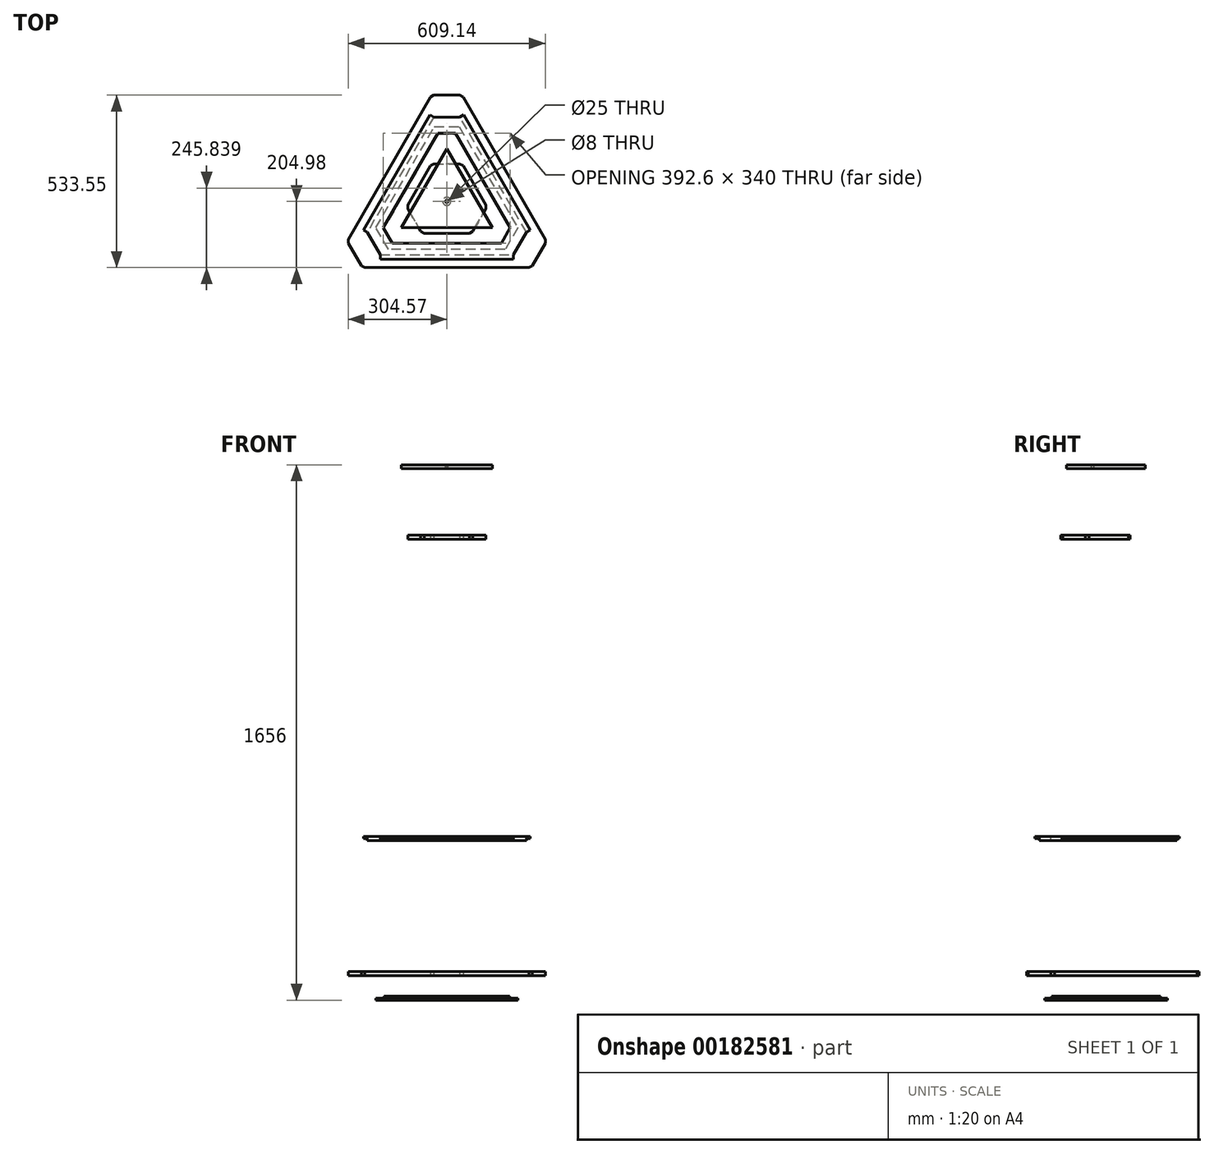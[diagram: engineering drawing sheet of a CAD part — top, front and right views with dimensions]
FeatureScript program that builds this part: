
annotation { "Feature Type Name" : "Feature", "Feature Type Description" : "" }
export const myFeature = defineFeature(function(context is Context, id is Id, definition is map)
    precondition{}
    {
        {
            var Q0;
            Q0=qCreatedBy(makeId("Front.planeOp"),FACE);
            var sketch = newSketch(context, id + "F0", { "sketchPlane" : qUnion([Q0])});
            skLineSegment(sketch, "E0", {"start": v(-375, 0) * mm, "end": v(375, 0) * mm});
            skLineSegment(sketch, "E1", {"start": v(0, 0) * mm, "end": v(0, 1650) * mm});
            skLineSegment(sketch, "E2", {"start": v(-150, 1650) * mm, "end": v(150, 1650) * mm});
            skSolve(sketch);
        }
        {
            var Q0;
            Q0=sQuery(id+"F0.wireOp",EDGE,"E2");
            cPoint(context, id + "F1", {"entities" : qUnion([Q0]), "parameter" : 0.5});
        }
        {
            var Q0;
            Q0=qCreatedBy(id+"F1",VERTEX);
            var Q1;
            Q1=sQuery(id+"F0.wireOp",EDGE,"E1");
            cPlane(context, id + "F2", {"entities" : qUnion([Q0, Q1]), "cplaneType" : CPlaneType.LINE_POINT, "offset" : 25 * mm, "width" : 150 * mm, "height" : 150 * mm});
        }
        {
            var Q0;
            Q0=qCreatedBy(makeId("Top.planeOp"),FACE);
            var sketch = newSketch(context, id + "F3", { "sketchPlane" : qUnion([Q0])});
            skCircle(sketch, "E3.cCircle", {"center": v(0, 0) * mm, "radius": 216.5 * mm, "construction": true});
            skLineSegment(sketch, "E3.0", {"start": v(375, -216.5) * mm, "end": v(-375, -216.5) * mm});
            skLineSegment(sketch, "E3.1", {"start": v(-375, -216.5) * mm, "end": v(0, 433.01) * mm});
            skLineSegment(sketch, "E3.2", {"start": v(0, 433.01) * mm, "end": v(375, -216.5) * mm});
            skPoint(sketch, "E3.0.midPoint", {"position": v(0, -216.5) * mm});
            skSolve(sketch);
        }
        {
            var Q0;
            Q0=qCreatedBy(id+"F2.planeOp",FACE);
            var sketch = newSketch(context, id + "F4", { "sketchPlane" : qUnion([Q0])});
            skCircle(sketch, "E4.cCircle", {"center": v(0, 0) * mm, "radius": 86.6 * mm, "construction": true});
            skLineSegment(sketch, "E4.0", {"start": v(150, -86.6) * mm, "end": v(-150, -86.6) * mm});
            skLineSegment(sketch, "E4.1", {"start": v(-150, -86.6) * mm, "end": v(0, 173.2) * mm});
            skLineSegment(sketch, "E4.2", {"start": v(0, 173.2) * mm, "end": v(150, -86.6) * mm});
            skPoint(sketch, "E4.0.midPoint", {"position": v(0, -86.6) * mm});
            skSolve(sketch);
        }
        {
            var Q0;
            Q0=makeQuery(id+"F3.imprint","IMPRINT",FACE,{"disambiguationData":[TD([[makeQuery(id+"F3.imprint","IMPRINT",EDGE,{"derivedFrom":sQuery(id+"F3.wireOp",EDGE,"E3.0")}),-1.0]])]});
            var Q1;
            Q1=makeQuery(id+"F4.imprint","IMPRINT",FACE,{"disambiguationData":[TD([[makeQuery(id+"F4.imprint","IMPRINT",EDGE,{"derivedFrom":sQuery(id+"F4.wireOp",EDGE,"E4.0")}),-1.0]])]});
            loft(context, id + "F5", {"sheetProfilesArray" : [{ "sheetProfileEntities" : qUnion([Q0]) }, { "sheetProfileEntities" : qUnion([Q1]) }]});
        }
        {
            var Q0;
            {var subQ0=sQuery(id+"F4.wireOp",EDGE,"E4.0");var subQ1=sQuery(id+"F4.wireOp",EDGE,"E4.1");var subQ2=sQuery(id+"F4.wireOp",EDGE,"E4.2");var subQ3=sQuery(id+"F3.wireOp",EDGE,"E3.0");var subQ4=sQuery(id+"F3.wireOp",EDGE,"E3.1");var subQ5=sQuery(id+"F3.wireOp",EDGE,"E3.2");Q0=makeQuery(id+"F5.opLoft","SWEPT_FACE",FACE,{"disambiguationData":[OSD([subQ3,subQ4,subQ5,subQ0,subQ1,subQ2]),TDD([makeQuery(id+"F3.imprint","INTERSECT",VERTEX,{"derivedFrom":[subQ3,subQ5]}),makeQuery(id+"F3.imprint","INTERSECT",VERTEX,{"derivedFrom":[subQ3,subQ4]}),makeQuery(id+"F3.imprint","IMPRINT",EDGE,{"derivedFrom":subQ3}),makeQuery(id+"F4.imprint","INTERSECT",VERTEX,{"derivedFrom":[subQ0,subQ2]}),makeQuery(id+"F4.imprint","INTERSECT",VERTEX,{"derivedFrom":[subQ0,subQ1]}),makeQuery(id+"F4.imprint","IMPRINT",EDGE,{"derivedFrom":subQ0})])]});}
            cPlane(context, id + "F6", {"entities" : qUnion([Q0]), "cplaneType" : CPlaneType.OFFSET, "offset" : 12 * mm, "oppositeDirection" : true, "width" : 150 * mm, "height" : 150 * mm});
        }
        {
            var Q0;
            Q0=qCreatedBy(id+"F6.planeOp",FACE);
            var sketch = newSketch(context, id + "F7", { "sketchPlane" : qUnion([Q0])});
            skCircle(sketch, "E5", {"center": v(0, 812.97) * mm, "radius": 960.24 * mm});
            skSolve(sketch);
        }
        {
            var Q0;
            Q0=qSketchRegion(id+"F7",true);
            extrude(context, id + "F8", {"entities" : qUnion([Q0]), "operationType" : NewBodyOperationType.REMOVE, "endBound" : BoundingType.THROUGH_ALL, "oppositeDirection" : true, "depth" : 25 * mm});
        }
        {
            var Q0;
            Q0=makeQuery(id+"F5.opLoft","CAP_FACE",FACE,{"disambiguationData":[OSD([makeQuery(id+"F4.imprint","IMPRINT",FACE,{"disambiguationData":[TD([[makeQuery(id+"F4.imprint","IMPRINT",EDGE,{"derivedFrom":sQuery(id+"F4.wireOp",EDGE,"E4.0")}),-1.0]])]})])],"isStart":true});
            var sketch = newSketch(context, id + "F9", { "sketchPlane" : qUnion([Q0])});
            skLineSegment(sketch, "E6", {"start": v(150, -86.6) * mm, "end": v(129.15, -74.57) * mm});
            skLineSegment(sketch, "E7", {"start": v(-150, -86.6) * mm, "end": v(-129.15, -74.57) * mm});
            skSolve(sketch);
        }
        {
            var Q0;
            Q0=makeQuery(id+"F5.opLoft","SWEPT_EDGE",EDGE,{"disambiguationData":[OSD([sQuery(id+"F3.wireOp",EDGE,"E3.0"),sQuery(id+"F3.wireOp",EDGE,"E3.1"),sQuery(id+"F4.wireOp",EDGE,"E4.0"),sQuery(id+"F4.wireOp",EDGE,"E4.1")])]});
            var Q1;
            Q1=sQuery(id+"F9.wireOp",EDGE,"E7");
            cPlane(context, id + "F10", {"entities" : qUnion([Q0, Q1]), "cplaneType" : CPlaneType.LINE_ANGLE, "offset" : 25 * mm, "angle" : 0 * degree, "width" : 150 * mm, "height" : 150 * mm});
        }
        {
            var Q0;
            Q0=makeQuery(id+"F5.opLoft","SWEPT_EDGE",EDGE,{"disambiguationData":[OSD([sQuery(id+"F3.wireOp",EDGE,"E3.0"),sQuery(id+"F3.wireOp",EDGE,"E3.2"),sQuery(id+"F4.wireOp",EDGE,"E4.0"),sQuery(id+"F4.wireOp",EDGE,"E4.2")])]});
            var Q1;
            Q1=sQuery(id+"F9.wireOp",EDGE,"E6");
            cPlane(context, id + "F11", {"entities" : qUnion([Q0, Q1]), "cplaneType" : CPlaneType.LINE_ANGLE, "offset" : 25 * mm, "angle" : 0 * degree, "width" : 150 * mm, "height" : 150 * mm});
        }
        {
            var Q0;
            Q0=qCreatedBy(id+"F11.planeOp",FACE);
            var sketch = newSketch(context, id + "F12", { "sketchPlane" : qUnion([Q0])});
            skCircle(sketch, "E8", {"center": v(304.07, 817.21) * mm, "radius": 870.23 * mm});
            skSolve(sketch);
        }
        {
            var Q0;
            Q0=qSketchRegion(id+"F12",true);
            extrude(context, id + "F13", {"entities" : qUnion([Q0]), "operationType" : NewBodyOperationType.REMOVE, "oppositeDirection" : true, "depth" : 25 * mm});
        }
        {
            var Q0;
            Q0=qCreatedBy(id+"F10.planeOp",FACE);
            var sketch = newSketch(context, id + "F14", { "sketchPlane" : qUnion([Q0])});
            skCircle(sketch, "E9", {"center": v(291.65, 811.12) * mm, "radius": 892.94 * mm});
            skSolve(sketch);
        }
        {
            var Q0;
            Q0=qSketchRegion(id+"F14",true);
            extrude(context, id + "F15", {"entities" : qUnion([Q0]), "operationType" : NewBodyOperationType.REMOVE, "depth" : 25 * mm});
        }
        {
            var Q0;
            Q0=makeQuery(id+"F8.boolean.opBoolean","COPY",FACE,{"derivedFrom":makeQuery(id+"F8.opExtrude","CAP_FACE",FACE,{"disambiguationData":[OSD([sQuery(id+"F7.wireOp",EDGE,"E5")])],"isStart":true})});
            cPlane(context, id + "F16", {"entities" : qUnion([Q0]), "cplaneType" : CPlaneType.OFFSET, "offset" : 6 * mm, "oppositeDirection" : true, "width" : 150 * mm, "height" : 150 * mm});
        }
        {
            var Q0;
            Q0=qCreatedBy(makeId("Front.planeOp"),FACE);
            var sketch = newSketch(context, id + "F17", { "sketchPlane" : qUnion([Q0])});
            skLineSegment(sketch, "E10.0.0", {"start": v(-354.15, 0) * mm, "end": v(-129.15, 1650) * mm, "construction": true});
            skLineSegment(sketch, "E10.0.1", {"start": v(-129.15, 1650) * mm, "end": v(129.15, 1650) * mm});
            skLineSegment(sketch, "E10.0.2", {"start": v(129.15, 1650) * mm, "end": v(354.15, 0) * mm, "construction": true});
            skLineSegment(sketch, "E11.0", {"start": v(-375, 0) * mm, "end": v(-150, 1650) * mm, "construction": true});
            skLineSegment(sketch, "E12.0", {"start": v(375, 0) * mm, "end": v(150, 1650) * mm, "construction": true});
            skLineSegment(sketch, "E13", {"start": v(83.17, 1400) * mm, "end": v(205.9, 500) * mm});
            skLineSegment(sketch, "E14", {"start": v(-83.17, 1400) * mm, "end": v(-205.9, 500) * mm});
            skLineSegment(sketch, "E15", {"start": v(83.17, 1400) * mm, "end": v(-83.17, 1400) * mm});
            skLineSegment(sketch, "E16", {"start": v(205.9, 500) * mm, "end": v(-205.9, 500) * mm});
            skLineSegment(sketch, "E17", {"start": v(274.07, 0) * mm, "end": v(267.26, 50) * mm});
            skLineSegment(sketch, "E18", {"start": v(267.26, 50) * mm, "end": v(-267.26, 50) * mm});
            skLineSegment(sketch, "E19", {"start": v(-267.26, 50) * mm, "end": v(-274.07, 0) * mm});
            skLineSegment(sketch, "E20", {"start": v(274.07, 0) * mm, "end": v(-274.07, 0) * mm});
            skSolve(sketch);
        }
        {
            var Q0;
            Q0=makeQuery(id+"F17.imprint","IMPRINT",FACE,{"disambiguationData":[TD([[makeQuery(id+"F17.imprint","IMPRINT",EDGE,{"derivedFrom":sQuery(id+"F17.wireOp",EDGE,"E13")}),-1.0]])]});
            var Q1;
            Q1=makeQuery(id+"F17.imprint","IMPRINT",FACE,{"disambiguationData":[TD([[makeQuery(id+"F17.imprint","IMPRINT",EDGE,{"derivedFrom":sQuery(id+"F17.wireOp",EDGE,"E17")}),1.0]])]});
            extrude(context, id + "F18", {"entities" : qUnion([Q0, Q1]), "operationType" : NewBodyOperationType.REMOVE, "endBound" : BoundingType.THROUGH_ALL, "depth" : 25 * mm});
        }
        {
            var Q0;
            Q0=qCreatedBy(makeId("Front.planeOp"),FACE);
            var sketch = newSketch(context, id + "F19", { "sketchPlane" : qUnion([Q0])});
            skLineSegment(sketch, "E21.0.0", {"start": v(274.07, 0) * mm, "end": v(267.26, 50) * mm});
            skLineSegment(sketch, "E21.0.1", {"start": v(267.26, 50) * mm, "end": v(-267.26, 50) * mm});
            skLineSegment(sketch, "E21.0.2", {"start": v(-267.26, 50) * mm, "end": v(-274.07, 0) * mm});
            skLineSegment(sketch, "E21.0.3", {"start": v(-274.07, 0) * mm, "end": v(-354.15, 0) * mm});
            skLineSegment(sketch, "E21.0.4", {"start": v(-354.15, 0) * mm, "end": v(-129.15, 1650) * mm});
            skLineSegment(sketch, "E21.0.5", {"start": v(-129.15, 1650) * mm, "end": v(129.15, 1650) * mm});
            skLineSegment(sketch, "E21.0.6", {"start": v(129.15, 1650) * mm, "end": v(354.15, 0) * mm});
            skLineSegment(sketch, "E21.0.7", {"start": v(354.15, 0) * mm, "end": v(274.07, 0) * mm});
            skLineSegment(sketch, "E22.0", {"start": v(205.9, 500) * mm, "end": v(83.17, 1400) * mm});
            skLineSegment(sketch, "E22.1", {"start": v(-205.9, 500) * mm, "end": v(-83.17, 1400) * mm});
            skLineSegment(sketch, "E23", {"start": v(205.9, 500) * mm, "end": v(-205.9, 500) * mm});
            skLineSegment(sketch, "E24", {"start": v(262.9, 82) * mm, "end": v(-262.9, 82) * mm});
            skLineSegment(sketch, "E25", {"start": v(80.44, 1420) * mm, "end": v(-80.44, 1420) * mm});
            skLineSegment(sketch, "E26", {"start": v(130.79, 1638) * mm, "end": v(-130.79, 1638) * mm});
            skLineSegment(sketch, "E27", {"start": v(78.8, 1432) * mm, "end": v(-78.8, 1432) * mm});
            skLineSegment(sketch, "E28", {"start": v(207.53, 488) * mm, "end": v(-207.53, 488) * mm});
            skLineSegment(sketch, "E29", {"start": v(264.53, 70) * mm, "end": v(-264.53, 70) * mm});
            skLineSegment(sketch, "E30", {"start": v(205.9, 500) * mm, "end": v(285.97, 500) * mm});
            skLineSegment(sketch, "E31", {"start": v(207.53, 488) * mm, "end": v(287.6, 488) * mm});
            skLineSegment(sketch, "E32", {"start": v(-207.53, 488) * mm, "end": v(-287.6, 488) * mm});
            skLineSegment(sketch, "E33", {"start": v(-205.9, 500) * mm, "end": v(-285.97, 500) * mm});
            skLineSegment(sketch, "E34", {"start": v(262.9, 82) * mm, "end": v(342.97, 82) * mm});
            skLineSegment(sketch, "E35", {"start": v(264.53, 70) * mm, "end": v(344.6, 70) * mm});
            skLineSegment(sketch, "E36", {"start": v(-264.53, 70) * mm, "end": v(-344.6, 70) * mm});
            skLineSegment(sketch, "E37", {"start": v(-262.9, 82) * mm, "end": v(-342.97, 82) * mm});
            skLineSegment(sketch, "E38", {"start": v(-80.44, 1420) * mm, "end": v(-160.51, 1420) * mm});
            skLineSegment(sketch, "E39", {"start": v(80.44, 1420) * mm, "end": v(160.51, 1420) * mm});
            skLineSegment(sketch, "E40", {"start": v(78.8, 1432) * mm, "end": v(158.88, 1432) * mm});
            skLineSegment(sketch, "E41", {"start": v(-78.8, 1432) * mm, "end": v(-158.88, 1432) * mm});
            skSolve(sketch);
        }
        {
            var Q0;
            Q0=makeQuery(id+"F18.boolean.opBoolean","COPY",FACE,{"derivedFrom":makeQuery(id+"F18.opExtrude","SWEPT_FACE",FACE,{"disambiguationData":[OSD([sQuery(id+"F17.wireOp",EDGE,"E16")])]})});
            var Q1;
            Q1=sQuery(id+"F19.wireOp",EDGE,"E23");
            cPlane(context, id + "F20", {"entities" : qUnion([Q0, Q1]), "cplaneType" : CPlaneType.LINE_ANGLE, "offset" : 25 * mm, "angle" : 0 * degree, "width" : 150 * mm, "height" : 150 * mm});
        }
        {
            var Q0;
            Q0=qCreatedBy(id+"F20.planeOp",FACE);
            var sketch = newSketch(context, id + "F21", { "sketchPlane" : qUnion([Q0])});
            skCircle(sketch, "E42.cCircle", {"center": v(0, 0) * mm, "radius": 165.1 * mm, "construction": true});
            skLineSegment(sketch, "E42.0", {"start": v(-285.97, 165.1) * mm, "end": v(285.97, 165.1) * mm, "construction": true});
            skLineSegment(sketch, "E42.1", {"start": v(285.97, 165.1) * mm, "end": v(0, -330.2) * mm, "construction": true});
            skLineSegment(sketch, "E42.2", {"start": v(0, -330.2) * mm, "end": v(-285.97, 165.1) * mm, "construction": true});
            skPoint(sketch, "E42.0.midPoint", {"position": v(0, 165.1) * mm});
            skLineSegment(sketch, "E43", {"start": v(-285.97, 165.1) * mm, "end": v(-285.97, 0) * mm, "construction": true});
            skLineSegment(sketch, "E44", {"start": v(-205.9, 0) * mm, "end": v(-205.9, 165.1) * mm, "construction": true});
            skLineSegment(sketch, "E45", {"start": v(-285.94, 171.12) * mm, "end": v(264.96, 171.12) * mm, "construction": true});
            skLineSegment(sketch, "E46", {"start": v(-205.9, 165.1) * mm, "end": v(-245.93, 95.76) * mm});
            skCircle(sketch, "E47.cCircle", {"center": v(0, 0) * mm, "radius": 171.12 * mm, "construction": true});
            skLineSegment(sketch, "E47.0", {"start": v(-296.4, 171.12) * mm, "end": v(296.4, 171.12) * mm, "construction": true});
            skLineSegment(sketch, "E47.1", {"start": v(296.4, 171.12) * mm, "end": v(0, -342.25) * mm, "construction": true});
            skLineSegment(sketch, "E47.2", {"start": v(0, -342.25) * mm, "end": v(-296.4, 171.12) * mm, "construction": true});
            skPoint(sketch, "E47.0.midPoint", {"position": v(0, 171.12) * mm});
            skLineSegment(sketch, "E48", {"start": v(-205.9, 165.1) * mm, "end": v(-205.9, 179.14) * mm});
            skLineSegment(sketch, "E49", {"start": v(-205.9, 179.14) * mm, "end": v(205.9, 179.14) * mm});
            skLineSegment(sketch, "E50", {"start": v(205.9, 165.1) * mm, "end": v(205.9, 179.14) * mm});
            skLineSegment(sketch, "E51.1.0", {"start": v(-245.93, 95.76) * mm, "end": v(-258.09, 88.74) * mm});
            skLineSegment(sketch, "E51.1.1", {"start": v(-52.2, -267.88) * mm, "end": v(-258.09, 88.74) * mm});
            skLineSegment(sketch, "E51.1.2", {"start": v(-40.04, -260.86) * mm, "end": v(-52.2, -267.88) * mm});
            skLineSegment(sketch, "E51.1.3", {"start": v(-40.04, -260.86) * mm, "end": v(40.04, -260.86) * mm});
            skLineSegment(sketch, "E51.2.0", {"start": v(40.04, -260.86) * mm, "end": v(52.2, -267.88) * mm});
            skLineSegment(sketch, "E51.2.1", {"start": v(258.09, 88.74) * mm, "end": v(52.2, -267.88) * mm});
            skLineSegment(sketch, "E51.2.2", {"start": v(245.93, 95.76) * mm, "end": v(258.09, 88.74) * mm});
            skLineSegment(sketch, "E51.2.3", {"start": v(245.93, 95.76) * mm, "end": v(205.9, 165.1) * mm});
            skLineSegment(sketch, "E52.0", {"start": v(196.3, 81.72) * mm, "end": v(27.38, -210.86) * mm});
            skLineSegment(sketch, "E52.1", {"start": v(-168.92, 129.14) * mm, "end": v(168.92, 129.14) * mm});
            skLineSegment(sketch, "E52.2", {"start": v(-168.92, 129.14) * mm, "end": v(-196.3, 81.72) * mm});
            skLineSegment(sketch, "E52.3", {"start": v(196.3, 81.72) * mm, "end": v(168.92, 129.14) * mm});
            skLineSegment(sketch, "E52.4", {"start": v(-27.38, -210.86) * mm, "end": v(-196.3, 81.72) * mm});
            skLineSegment(sketch, "E52.5", {"start": v(-27.38, -210.86) * mm, "end": v(27.38, -210.86) * mm});
            skSolve(sketch);
        }
        {
            var Q0;
            Q0=makeQuery(id+"F18.boolean.opBoolean","COPY",FACE,{"derivedFrom":makeQuery(id+"F18.opExtrude","SWEPT_FACE",FACE,{"disambiguationData":[OSD([sQuery(id+"F17.wireOp",EDGE,"E16")])]})});
            var Q1;
            Q1=sQuery(id+"F19.wireOp",VERTEX,"E31.start");
            cPlane(context, id + "F22", {"entities" : qUnion([Q0, Q1]), "cplaneType" : CPlaneType.PLANE_POINT, "offset" : 25 * mm, "width" : 150 * mm, "height" : 150 * mm});
        }
        {
            var Q0;
            Q0=makeQuery(id+"F18.boolean.opBoolean","COPY",FACE,{"derivedFrom":makeQuery(id+"F18.opExtrude","SWEPT_FACE",FACE,{"disambiguationData":[OSD([sQuery(id+"F17.wireOp",EDGE,"E18")])]})});
            var Q1;
            Q1=sQuery(id+"F19.wireOp",VERTEX,"E29.end");
            cPlane(context, id + "F23", {"entities" : qUnion([Q0, Q1]), "cplaneType" : CPlaneType.PLANE_POINT, "offset" : 25 * mm, "width" : 150 * mm, "height" : 150 * mm});
        }
        {
            var Q0;
            Q0=qCreatedBy(id+"F23.planeOp",FACE);
            var sketch = newSketch(context, id + "F24", { "sketchPlane" : qUnion([Q0])});
            skCircle(sketch, "E53.cCircle", {"center": v(0, 0) * mm, "radius": 198.96 * mm, "construction": true});
            skLineSegment(sketch, "E53.0", {"start": v(-344.6, 198.96) * mm, "end": v(344.6, 198.96) * mm, "construction": true});
            skLineSegment(sketch, "E53.1", {"start": v(344.6, 198.96) * mm, "end": v(0, -397.92) * mm, "construction": true});
            skLineSegment(sketch, "E53.2", {"start": v(0, -397.92) * mm, "end": v(-344.6, 198.96) * mm, "construction": true});
            skPoint(sketch, "E53.0.midPoint", {"position": v(0, 198.96) * mm});
            skCircle(sketch, "E54.cCircle", {"center": v(0, 0) * mm, "radius": 204.98 * mm, "construction": true});
            skLineSegment(sketch, "E54.0", {"start": v(-355.03, 204.98) * mm, "end": v(355.03, 204.98) * mm, "construction": true});
            skLineSegment(sketch, "E54.1", {"start": v(355.03, 204.98) * mm, "end": v(0, -409.95) * mm, "construction": true});
            skLineSegment(sketch, "E54.2", {"start": v(0, -409.95) * mm, "end": v(-355.03, 204.98) * mm, "construction": true});
            skPoint(sketch, "E54.0.midPoint", {"position": v(0, 204.98) * mm});
            skLineSegment(sketch, "E55.0", {"start": v(264.53, 0) * mm, "end": v(-264.53, 0) * mm, "construction": true});
            skLineSegment(sketch, "E56", {"start": v(-344.6, 198.96) * mm, "end": v(-344.6, 0) * mm, "construction": true});
            skLineSegment(sketch, "E57", {"start": v(-264.53, 0) * mm, "end": v(-264.53, 198.96) * mm, "construction": true});
            skLineSegment(sketch, "E58", {"start": v(-264.53, 198.96) * mm, "end": v(-254.1, 204.98) * mm});
            skLineSegment(sketch, "E59", {"start": v(-264.53, 198.96) * mm, "end": v(-304.57, 129.6) * mm});
            skLineSegment(sketch, "E60", {"start": v(-304.57, 129.6) * mm, "end": v(-304.57, 117.57) * mm});
            skLineSegment(sketch, "E61.1.0", {"start": v(-40.04, -328.57) * mm, "end": v(-50.46, -322.55) * mm});
            skLineSegment(sketch, "E61.1.1", {"start": v(-40.04, -328.57) * mm, "end": v(40.04, -328.57) * mm});
            skLineSegment(sketch, "E61.1.2", {"start": v(40.04, -328.57) * mm, "end": v(50.46, -322.55) * mm});
            skLineSegment(sketch, "E61.2.0", {"start": v(304.57, 129.6) * mm, "end": v(304.57, 117.57) * mm});
            skLineSegment(sketch, "E61.2.1", {"start": v(304.57, 129.6) * mm, "end": v(264.53, 198.96) * mm});
            skLineSegment(sketch, "E61.2.2", {"start": v(264.53, 198.96) * mm, "end": v(254.1, 204.98) * mm});
            skLineSegment(sketch, "E62", {"start": v(-304.57, 117.57) * mm, "end": v(-50.46, -322.55) * mm});
            skLineSegment(sketch, "E63", {"start": v(50.46, -322.55) * mm, "end": v(304.57, 117.57) * mm});
            skLineSegment(sketch, "E64", {"start": v(254.1, 204.98) * mm, "end": v(-254.1, 204.98) * mm});
            skSolve(sketch);
        }
        {
            var Q0;
            Q0=makeQuery(id+"F18.boolean.opBoolean","COPY",FACE,{"derivedFrom":makeQuery(id+"F18.opExtrude","SWEPT_FACE",FACE,{"disambiguationData":[OSD([sQuery(id+"F17.wireOp",EDGE,"E18")])]})});
            var Q1;
            Q1=sQuery(id+"F19.wireOp",VERTEX,"E34.start");
            cPlane(context, id + "F25", {"entities" : qUnion([Q0, Q1]), "cplaneType" : CPlaneType.PLANE_POINT, "offset" : 25 * mm, "width" : 150 * mm, "height" : 150 * mm});
        }
        {
            var Q0;
            Q0=qCreatedBy(id+"F25.planeOp",FACE);
            var sketch = newSketch(context, id + "F26", { "sketchPlane" : qUnion([Q0])});
            skLineSegment(sketch, "E65.0", {"start": v(262.9, 0) * mm, "end": v(-262.9, 0) * mm, "construction": true});
            skCircle(sketch, "E66.cCircle", {"center": v(0, 0) * mm, "radius": 204.03 * mm, "construction": true});
            skLineSegment(sketch, "E66.0", {"start": v(-353.4, 204.03) * mm, "end": v(353.4, 204.03) * mm, "construction": true});
            skLineSegment(sketch, "E66.1", {"start": v(353.4, 204.03) * mm, "end": v(0, -408.06) * mm, "construction": true});
            skLineSegment(sketch, "E66.2", {"start": v(0, -408.06) * mm, "end": v(-353.4, 204.03) * mm, "construction": true});
            skPoint(sketch, "E66.0.midPoint", {"position": v(0, 204.03) * mm});
            skCircle(sketch, "E67.cCircle", {"center": v(0, 0) * mm, "radius": 198.01 * mm, "construction": true});
            skLineSegment(sketch, "E67.0", {"start": v(-342.97, 198.01) * mm, "end": v(342.97, 198.01) * mm, "construction": true});
            skLineSegment(sketch, "E67.1", {"start": v(342.97, 198.01) * mm, "end": v(0, -396.03) * mm, "construction": true});
            skLineSegment(sketch, "E67.2", {"start": v(0, -396.03) * mm, "end": v(-342.97, 198.01) * mm, "construction": true});
            skPoint(sketch, "E67.0.midPoint", {"position": v(0, 198.01) * mm});
            skLineSegment(sketch, "E68", {"start": v(-342.97, 198.01) * mm, "end": v(-342.97, 0) * mm, "construction": true});
            skLineSegment(sketch, "E69", {"start": v(-262.9, 0) * mm, "end": v(-262.9, 198.01) * mm, "construction": true});
            skLineSegment(sketch, "E70", {"start": v(-262.9, 198.01) * mm, "end": v(-252.47, 204.03) * mm});
            skLineSegment(sketch, "E71", {"start": v(-262.9, 198.01) * mm, "end": v(-302.93, 128.67) * mm});
            skLineSegment(sketch, "E72", {"start": v(-302.93, 128.67) * mm, "end": v(-302.93, 116.63) * mm});
            skLineSegment(sketch, "E73.1.0", {"start": v(40.04, -326.68) * mm, "end": v(50.46, -320.66) * mm});
            skLineSegment(sketch, "E73.1.1", {"start": v(-40.04, -326.68) * mm, "end": v(40.04, -326.68) * mm});
            skLineSegment(sketch, "E73.1.2", {"start": v(-40.04, -326.68) * mm, "end": v(-50.46, -320.66) * mm});
            skLineSegment(sketch, "E73.2.0", {"start": v(262.9, 198.01) * mm, "end": v(252.47, 204.03) * mm});
            skLineSegment(sketch, "E73.2.1", {"start": v(302.93, 128.67) * mm, "end": v(262.9, 198.01) * mm});
            skLineSegment(sketch, "E73.2.2", {"start": v(302.93, 128.67) * mm, "end": v(302.93, 116.63) * mm});
            skLineSegment(sketch, "E74", {"start": v(-50.46, -320.66) * mm, "end": v(-302.93, 116.63) * mm});
            skLineSegment(sketch, "E75", {"start": v(-252.47, 204.03) * mm, "end": v(252.47, 204.03) * mm});
            skLineSegment(sketch, "E76", {"start": v(302.93, 116.63) * mm, "end": v(50.46, -320.66) * mm});
            skSolve(sketch);
        }
        {
            var Q0;
            Q0=sQuery(id+"F19.wireOp",VERTEX,"E39.start");
            var Q1;
            {var subQ0=sQuery(id+"F9.wireOp",EDGE,"E6");Q1=makeQuery(id+"F9.imprint","IMPRINT",FACE,{"disambiguationData":[TD([[makeQuery(id+"F9.imprint","IMPRINT",EDGE,{"derivedFrom":subQ0}),1.0]])]});}
            cPlane(context, id + "F27", {"entities" : qUnion([Q0, Q1]), "cplaneType" : CPlaneType.PLANE_POINT, "offset" : 25 * mm, "width" : 150 * mm, "height" : 150 * mm});
        }
        {
            var Q0;
            Q0=qCreatedBy(id+"F27.planeOp",FACE);
            var sketch = newSketch(context, id + "F28", { "sketchPlane" : qUnion([Q0])});
            skLineSegment(sketch, "E77.0", {"start": v(80.44, 0) * mm, "end": v(-80.44, 0) * mm, "construction": true});
            skCircle(sketch, "E78.cCircle", {"center": v(0, 0) * mm, "radius": 98.7 * mm, "construction": true});
            skLineSegment(sketch, "E78.0", {"start": v(170.94, -98.7) * mm, "end": v(-170.94, -98.7) * mm, "construction": true});
            skLineSegment(sketch, "E78.1", {"start": v(-170.94, -98.7) * mm, "end": v(0, 197.38) * mm, "construction": true});
            skLineSegment(sketch, "E78.2", {"start": v(0, 197.38) * mm, "end": v(170.94, -98.7) * mm, "construction": true});
            skPoint(sketch, "E78.0.midPoint", {"position": v(0, -98.7) * mm});
            skCircle(sketch, "E79.cCircle", {"center": v(0, 0) * mm, "radius": 92.67 * mm, "construction": true});
            skLineSegment(sketch, "E79.0", {"start": v(160.51, -92.67) * mm, "end": v(-160.51, -92.67) * mm, "construction": true});
            skLineSegment(sketch, "E79.1", {"start": v(-160.51, -92.67) * mm, "end": v(0, 185.35) * mm, "construction": true});
            skLineSegment(sketch, "E79.2", {"start": v(0, 185.35) * mm, "end": v(160.51, -92.67) * mm, "construction": true});
            skPoint(sketch, "E79.0.midPoint", {"position": v(0, -92.67) * mm});
            skLineSegment(sketch, "E80", {"start": v(-160.51, -92.67) * mm, "end": v(-160.51, 0) * mm, "construction": true});
            skLineSegment(sketch, "E81", {"start": v(-80.44, 0) * mm, "end": v(-80.44, -92.67) * mm, "construction": true});
            skLineSegment(sketch, "E82", {"start": v(-80.44, -92.67) * mm, "end": v(-70.01, -98.7) * mm});
            skLineSegment(sketch, "E83", {"start": v(-80.44, -92.67) * mm, "end": v(-120.48, -23.32) * mm});
            skLineSegment(sketch, "E84", {"start": v(-120.48, -23.32) * mm, "end": v(-120.48, -11.29) * mm});
            skLineSegment(sketch, "E85.1.0", {"start": v(120.48, -23.32) * mm, "end": v(120.48, -11.29) * mm});
            skLineSegment(sketch, "E85.1.1", {"start": v(120.48, -23.32) * mm, "end": v(80.44, -92.67) * mm});
            skLineSegment(sketch, "E85.1.2", {"start": v(80.44, -92.67) * mm, "end": v(70.01, -98.7) * mm});
            skLineSegment(sketch, "E85.2.0", {"start": v(-40.04, 116) * mm, "end": v(-50.46, 109.98) * mm});
            skLineSegment(sketch, "E85.2.1", {"start": v(-40.04, 116) * mm, "end": v(40.04, 116) * mm});
            skLineSegment(sketch, "E85.2.2", {"start": v(40.04, 116) * mm, "end": v(50.46, 109.98) * mm});
            skLineSegment(sketch, "E86", {"start": v(-50.46, 109.98) * mm, "end": v(-120.48, -11.29) * mm});
            skLineSegment(sketch, "E87", {"start": v(50.46, 109.98) * mm, "end": v(120.48, -11.29) * mm});
            skLineSegment(sketch, "E88", {"start": v(70.01, -98.7) * mm, "end": v(-70.01, -98.7) * mm});
            skSolve(sketch);
        }
        {
            var Q0;
            {var subQ0=sQuery(id+"F9.wireOp",EDGE,"E6");Q0=makeQuery(id+"F9.imprint","IMPRINT",FACE,{"disambiguationData":[TD([[makeQuery(id+"F9.imprint","IMPRINT",EDGE,{"derivedFrom":subQ0}),1.0]])]});}
            var Q1;
            Q1=sQuery(id+"F19.wireOp",VERTEX,"E27.end");
            cPlane(context, id + "F29", {"entities" : qUnion([Q0, Q1]), "cplaneType" : CPlaneType.PLANE_POINT, "offset" : 25 * mm, "width" : 150 * mm, "height" : 150 * mm});
        }
        {
            var Q0;
            Q0=qCreatedBy(id+"F29.planeOp",FACE);
            var sketch = newSketch(context, id + "F30", { "sketchPlane" : qUnion([Q0])});
            skLineSegment(sketch, "E89.0", {"start": v(78.8, 0) * mm, "end": v(-78.8, 0) * mm, "construction": true});
            skCircle(sketch, "E90.cCircle", {"center": v(0, 0) * mm, "radius": 91.73 * mm, "construction": true});
            skPoint(sketch, "E90.cCircle.perimeterSnap0", {"position": v(0, 0) * mm});
            skLineSegment(sketch, "E90.0", {"start": v(158.88, -91.73) * mm, "end": v(-158.88, -91.73) * mm, "construction": true});
            skLineSegment(sketch, "E90.1", {"start": v(-158.88, -91.73) * mm, "end": v(0, 183.46) * mm, "construction": true});
            skLineSegment(sketch, "E90.2", {"start": v(0, 183.46) * mm, "end": v(158.88, -91.73) * mm, "construction": true});
            skPoint(sketch, "E90.0.midPoint", {"position": v(0, -91.73) * mm});
            skPoint(sketch, "E90.0.midPoint.positionSnap0", {"position": v(0, 0) * mm});
            skCircle(sketch, "E91.cCircle", {"center": v(0, 0) * mm, "radius": 97.75 * mm, "construction": true});
            skLineSegment(sketch, "E91.0", {"start": v(169.3, -97.75) * mm, "end": v(-169.3, -97.75) * mm, "construction": true});
            skLineSegment(sketch, "E91.1", {"start": v(-169.3, -97.75) * mm, "end": v(0, 195.5) * mm, "construction": true});
            skLineSegment(sketch, "E91.2", {"start": v(0, 195.5) * mm, "end": v(169.3, -97.75) * mm, "construction": true});
            skPoint(sketch, "E91.0.midPoint", {"position": v(0, -97.75) * mm});
            skLineSegment(sketch, "E92", {"start": v(-158.88, -91.73) * mm, "end": v(-158.88, 0) * mm, "construction": true});
            skLineSegment(sketch, "E93", {"start": v(-78.8, 0) * mm, "end": v(-78.8, -91.73) * mm, "construction": true});
            skLineSegment(sketch, "E94", {"start": v(-78.8, -91.73) * mm, "end": v(-68.38, -97.75) * mm});
            skLineSegment(sketch, "E95", {"start": v(-78.8, -91.73) * mm, "end": v(-118.84, -22.38) * mm});
            skLineSegment(sketch, "E96", {"start": v(-118.84, -22.38) * mm, "end": v(-118.84, -10.34) * mm});
            skLineSegment(sketch, "E97.1.0", {"start": v(118.84, -22.38) * mm, "end": v(118.84, -10.34) * mm});
            skLineSegment(sketch, "E97.1.1", {"start": v(118.84, -22.38) * mm, "end": v(78.8, -91.73) * mm});
            skLineSegment(sketch, "E97.1.2", {"start": v(78.8, -91.73) * mm, "end": v(68.38, -97.75) * mm});
            skLineSegment(sketch, "E97.2.0", {"start": v(-40.04, 114.1) * mm, "end": v(-50.46, 108.1) * mm});
            skLineSegment(sketch, "E97.2.1", {"start": v(-40.04, 114.1) * mm, "end": v(40.04, 114.1) * mm});
            skLineSegment(sketch, "E97.2.2", {"start": v(40.04, 114.1) * mm, "end": v(50.46, 108.1) * mm});
            skLineSegment(sketch, "E98", {"start": v(-68.38, -97.75) * mm, "end": v(68.38, -97.75) * mm});
            skLineSegment(sketch, "E99", {"start": v(50.46, 108.1) * mm, "end": v(118.84, -10.34) * mm});
            skLineSegment(sketch, "E100", {"start": v(-50.46, 108.1) * mm, "end": v(-118.84, -10.34) * mm});
            skSolve(sketch);
        }
        {
            var Q0;
            {var subQ0=sQuery(id+"F9.wireOp",EDGE,"E6");Q0=makeQuery(id+"F9.imprint","IMPRINT",FACE,{"disambiguationData":[TD([[makeQuery(id+"F9.imprint","IMPRINT",EDGE,{"derivedFrom":subQ0}),1.0]])]});}
            var Q1;
            Q1=sQuery(id+"F19.wireOp",VERTEX,"E26.end");
            cPlane(context, id + "F31", {"entities" : qUnion([Q0, Q1]), "cplaneType" : CPlaneType.PLANE_POINT, "offset" : 25 * mm, "width" : 150 * mm, "height" : 150 * mm});
        }
        {
            var Q0;
            Q0=qCreatedBy(id+"F31.planeOp",FACE);
            var sketch = newSketch(context, id + "F32", { "sketchPlane" : qUnion([Q0])});
            skLineSegment(sketch, "E101.0", {"start": v(130.79, 0) * mm, "end": v(-130.79, 0) * mm, "construction": true});
            skCircle(sketch, "E102.cCircle", {"center": v(0, 0) * mm, "radius": 81.53 * mm, "construction": true});
            skPoint(sketch, "E102.cCircle.perimeterSnap0", {"position": v(0, 0) * mm});
            skLineSegment(sketch, "E102.0", {"start": v(141.21, -81.53) * mm, "end": v(-141.21, -81.53) * mm});
            skLineSegment(sketch, "E102.1", {"start": v(-141.21, -81.53) * mm, "end": v(0, 163.06) * mm});
            skLineSegment(sketch, "E102.2", {"start": v(0, 163.06) * mm, "end": v(141.21, -81.53) * mm});
            skPoint(sketch, "E102.0.midPoint", {"position": v(0, -81.53) * mm});
            skPoint(sketch, "E102.0.midPoint.positionSnap0", {"position": v(0, 0) * mm});
            skSolve(sketch);
        }
        {
            var Q0;
            {var subQ0=sQuery(id+"F9.wireOp",EDGE,"E6");Q0=makeQuery(id+"F9.imprint","IMPRINT",FACE,{"disambiguationData":[TD([[makeQuery(id+"F9.imprint","IMPRINT",EDGE,{"derivedFrom":subQ0}),1.0]])]});}
            var Q1;
            Q1=sQuery(id+"F19.wireOp",VERTEX,"E21.0.6.start");
            cPlane(context, id + "F33", {"entities" : qUnion([Q0, Q1]), "cplaneType" : CPlaneType.PLANE_POINT, "offset" : 25 * mm, "width" : 150 * mm, "height" : 150 * mm});
        }
        {
            var Q0;
            Q0=qCreatedBy(makeId("Top.planeOp"),FACE);
            var sketch = newSketch(context, id + "F34", { "sketchPlane" : qUnion([Q0])});
            skCircle(sketch, "E103", {"center": v(0, 0) * mm, "radius": 537.08 * mm});
            skSolve(sketch);
        }
        {
            var Q0;
            Q0=qSketchRegion(id+"F34",true);
            extrude(context, id + "F35", {"entities" : qUnion([Q0]), "operationType" : NewBodyOperationType.REMOVE, "endBound" : BoundingType.THROUGH_ALL, "depth" : 25 * mm});
        }
        {
            var Q0;
            Q0=qCreatedBy(id+"F33.planeOp",FACE);
            var sketch = newSketch(context, id + "F36", { "sketchPlane" : qUnion([Q0])});
            skCircle(sketch, "E104.cCircle", {"center": v(0, 0) * mm, "radius": 80.58 * mm, "construction": true});
            skLineSegment(sketch, "E104.0", {"start": v(139.58, -80.58) * mm, "end": v(-139.58, -80.58) * mm});
            skLineSegment(sketch, "E104.1", {"start": v(-139.58, -80.58) * mm, "end": v(0, 161.17) * mm});
            skLineSegment(sketch, "E104.2", {"start": v(0, 161.17) * mm, "end": v(139.58, -80.58) * mm});
            skPoint(sketch, "E104.0.midPoint", {"position": v(0, -80.58) * mm});
            skSolve(sketch);
        }
        {
            var Q0;
            Q0=makeQuery(id+"F32.imprint","IMPRINT",FACE,{"disambiguationData":[TD([[makeQuery(id+"F32.imprint","IMPRINT",EDGE,{"derivedFrom":sQuery(id+"F32.wireOp",EDGE,"E102.0")}),-1.0]])]});
            var Q1;
            Q1=makeQuery(id+"F36.imprint","IMPRINT",FACE,{"disambiguationData":[TD([[makeQuery(id+"F36.imprint","IMPRINT",EDGE,{"derivedFrom":sQuery(id+"F36.wireOp",EDGE,"E104.0")}),-1.0]])]});
            loft(context, id + "F37", {"sheetProfilesArray" : [{ "sheetProfileEntities" : qUnion([Q0]) }, { "sheetProfileEntities" : qUnion([Q1]) }]});
        }
        {
            var Q0;
            Q0=makeQuery(id+"F28.imprint","IMPRINT",FACE,{"disambiguationData":[TD([[makeQuery(id+"F28.imprint","IMPRINT",EDGE,{"derivedFrom":sQuery(id+"F28.wireOp",EDGE,"E82")}),1.0]])]});
            var Q1;
            Q1=makeQuery(id+"F30.imprint","IMPRINT",FACE,{"disambiguationData":[TD([[makeQuery(id+"F30.imprint","IMPRINT",EDGE,{"derivedFrom":sQuery(id+"F30.wireOp",EDGE,"E94")}),1.0]])]});
            loft(context, id + "F38", {"sheetProfilesArray" : [{ "sheetProfileEntities" : qUnion([Q0]) }, { "sheetProfileEntities" : qUnion([Q1]) }]});
        }
        {
            var Q0;
            Q0=makeQuery(id+"F26.imprint","IMPRINT",FACE,{"disambiguationData":[TD([[makeQuery(id+"F26.imprint","IMPRINT",EDGE,{"derivedFrom":sQuery(id+"F26.wireOp",EDGE,"E70")}),-1.0]])]});
            var Q1;
            Q1=makeQuery(id+"F24.imprint","IMPRINT",FACE,{"disambiguationData":[TD([[makeQuery(id+"F24.imprint","IMPRINT",EDGE,{"derivedFrom":sQuery(id+"F24.wireOp",EDGE,"E58")}),-1.0]])]});
            loft(context, id + "F39", {"sheetProfilesArray" : [{ "sheetProfileEntities" : qUnion([Q0]) }, { "sheetProfileEntities" : qUnion([Q1]) }]});
        }
        {
            var Q0;
            Q0=makeQuery(id+"F37.opLoft","CAP_FACE",FACE,{"disambiguationData":[OSD([makeQuery(id+"F36.imprint","IMPRINT",FACE,{"disambiguationData":[TD([[makeQuery(id+"F36.imprint","IMPRINT",EDGE,{"derivedFrom":sQuery(id+"F36.wireOp",EDGE,"E104.0")}),-1.0]])]})])],"isStart":true});
            var sketch = newSketch(context, id + "F40", { "sketchPlane" : qUnion([Q0])});
            skCircle(sketch, "E105", {"center": v(0, 0) * mm, "radius": 4 * mm});
            skSolve(sketch);
        }
        {
            var Q0;
            Q0=qSketchRegion(id+"F40",true);
            extrude(context, id + "F41", {"entities" : qUnion([Q0]), "operationType" : NewBodyOperationType.REMOVE, "endBound" : BoundingType.UP_TO_NEXT, "oppositeDirection" : true, "depth" : 25 * mm});
        }
        {
            var Q0;
            Q0=makeQuery(id+"F37.opLoft","CAP_FACE",FACE,{"disambiguationData":[OSD([makeQuery(id+"F32.imprint","IMPRINT",FACE,{"disambiguationData":[TD([[makeQuery(id+"F32.imprint","IMPRINT",EDGE,{"derivedFrom":sQuery(id+"F32.wireOp",EDGE,"E102.0")}),-1.0]])]})])],"isStart":true});
            var sketch = newSketch(context, id + "F42", { "sketchPlane" : qUnion([Q0])});
            skLineSegment(sketch, "E106.0", {"start": v(0, -163.06) * mm, "end": v(-141.21, 81.53) * mm});
            skLineSegment(sketch, "E107.0", {"start": v(141.21, 81.53) * mm, "end": v(0, -163.06) * mm});
            skLineSegment(sketch, "E108.0", {"start": v(-141.21, 81.53) * mm, "end": v(141.21, 81.53) * mm});
            skCircle(sketch, "E109.0", {"center": v(0, 0) * mm, "radius": 4 * mm});
            skSolve(sketch);
        }
        {
            var Q0;
            Q0 = qSketchRegion(id + "F42", true);
            var Q1;
            Q1=makeQuery(id+"F37.opLoft","CAP_FACE",FACE,{"disambiguationData":[OSD([makeQuery(id+"F36.imprint","IMPRINT",FACE,{"disambiguationData":[TD([[makeQuery(id+"F36.imprint","IMPRINT",EDGE,{"derivedFrom":sQuery(id+"F36.wireOp",EDGE,"E104.0")}),-1.0]])]})])],"isStart":true});
            extrude(context, id + "F43", {"entities" : qUnion([Q0]), "operationType" : NewBodyOperationType.ADD, "endBound" : BoundingType.UP_TO_SURFACE, "oppositeDirection" : true, "endBoundEntityFace" : qUnion([Q1]), "depth" : 25 * mm});
        }
        {
            var Q0;
            Q0=makeQuery(id+"F38.opLoft","CAP_FACE",FACE,{"disambiguationData":[OSD([makeQuery(id+"F28.imprint","IMPRINT",FACE,{"disambiguationData":[TD([[makeQuery(id+"F28.imprint","IMPRINT",EDGE,{"derivedFrom":sQuery(id+"F28.wireOp",EDGE,"E82")}),1.0]])]})])],"isStart":true});
            var sketch = newSketch(context, id + "F44", { "sketchPlane" : qUnion([Q0])});
            skLineSegment(sketch, "E110.0", {"start": v(80.44, 92.67) * mm, "end": v(120.48, 23.32) * mm});
            skLineSegment(sketch, "E111.0", {"start": v(120.48, 23.32) * mm, "end": v(120.48, 11.29) * mm});
            skLineSegment(sketch, "E112.0", {"start": v(120.48, 11.29) * mm, "end": v(50.46, -109.98) * mm});
            skLineSegment(sketch, "E113.0", {"start": v(70.01, 98.7) * mm, "end": v(80.44, 92.67) * mm});
            skLineSegment(sketch, "E114.0", {"start": v(-70.01, 98.7) * mm, "end": v(70.01, 98.7) * mm});
            skLineSegment(sketch, "E115.0", {"start": v(50.46, -109.98) * mm, "end": v(40.04, -116) * mm});
            skLineSegment(sketch, "E116.0", {"start": v(40.04, -116) * mm, "end": v(-40.04, -116) * mm});
            skLineSegment(sketch, "E117.0", {"start": v(-40.04, -116) * mm, "end": v(-50.46, -109.98) * mm});
            skLineSegment(sketch, "E118.0", {"start": v(-50.46, -109.98) * mm, "end": v(-120.48, 11.29) * mm});
            skLineSegment(sketch, "E119.0", {"start": v(-80.44, 92.67) * mm, "end": v(-70.01, 98.7) * mm});
            skLineSegment(sketch, "E120.0", {"start": v(-120.48, 23.32) * mm, "end": v(-80.44, 92.67) * mm});
            skLineSegment(sketch, "E121.0", {"start": v(-120.48, 11.29) * mm, "end": v(-120.48, 23.32) * mm});
            skSolve(sketch);
        }
        {
            var Q0;
            Q0 = qSketchRegion(id + "F44", true);
            var Q1;
            Q1=makeQuery(id+"F38.opLoft","CAP_FACE",FACE,{"disambiguationData":[OSD([makeQuery(id+"F30.imprint","IMPRINT",FACE,{"disambiguationData":[TD([[makeQuery(id+"F30.imprint","IMPRINT",EDGE,{"derivedFrom":sQuery(id+"F30.wireOp",EDGE,"E94")}),1.0]])]})])],"isStart":true});
            extrude(context, id + "F45", {"entities" : qUnion([Q0]), "operationType" : NewBodyOperationType.ADD, "endBound" : BoundingType.UP_TO_SURFACE, "oppositeDirection" : true, "endBoundEntityFace" : qUnion([Q1]), "depth" : 25 * mm});
        }
        {
            var Q0;
            Q0=makeQuery(id+"F39.opLoft","CAP_FACE",FACE,{"disambiguationData":[OSD([makeQuery(id+"F24.imprint","IMPRINT",FACE,{"disambiguationData":[TD([[makeQuery(id+"F24.imprint","IMPRINT",EDGE,{"derivedFrom":sQuery(id+"F24.wireOp",EDGE,"E58")}),-1.0]])]})])],"isStart":true});
            var sketch = newSketch(context, id + "F46", { "sketchPlane" : qUnion([Q0])});
            skLineSegment(sketch, "E122.0.0", {"start": v(-254.1, 204.98) * mm, "end": v(-264.53, 198.96) * mm});
            skLineSegment(sketch, "E122.0.1", {"start": v(-264.53, 198.96) * mm, "end": v(-304.57, 129.6) * mm});
            skLineSegment(sketch, "E122.0.2", {"start": v(-304.57, 129.6) * mm, "end": v(-304.57, 117.57) * mm});
            skLineSegment(sketch, "E122.0.3", {"start": v(-304.57, 117.57) * mm, "end": v(-50.46, -322.55) * mm});
            skLineSegment(sketch, "E122.0.4", {"start": v(-50.46, -322.55) * mm, "end": v(-40.04, -328.57) * mm});
            skLineSegment(sketch, "E122.0.5", {"start": v(-40.04, -328.57) * mm, "end": v(40.04, -328.57) * mm});
            skLineSegment(sketch, "E122.0.6", {"start": v(40.04, -328.57) * mm, "end": v(50.46, -322.55) * mm});
            skLineSegment(sketch, "E122.0.7", {"start": v(50.46, -322.55) * mm, "end": v(304.57, 117.57) * mm});
            skLineSegment(sketch, "E122.0.8", {"start": v(304.57, 117.57) * mm, "end": v(304.57, 129.6) * mm});
            skLineSegment(sketch, "E122.0.9", {"start": v(304.57, 129.6) * mm, "end": v(264.53, 198.96) * mm});
            skLineSegment(sketch, "E122.0.10", {"start": v(264.53, 198.96) * mm, "end": v(254.1, 204.98) * mm});
            skLineSegment(sketch, "E122.0.11", {"start": v(254.1, 204.98) * mm, "end": v(-254.1, 204.98) * mm});
            skSolve(sketch);
        }
        {
            var Q0;
            Q0 = qSketchRegion(id + "F46", true);
            var Q1;
            Q1=makeQuery(id+"F39.opLoft","CAP_FACE",FACE,{"disambiguationData":[OSD([makeQuery(id+"F26.imprint","IMPRINT",FACE,{"disambiguationData":[TD([[makeQuery(id+"F26.imprint","IMPRINT",EDGE,{"derivedFrom":sQuery(id+"F26.wireOp",EDGE,"E70")}),-1.0]])]})])],"isStart":true});
            extrude(context, id + "F47", {"entities" : qUnion([Q0]), "operationType" : NewBodyOperationType.ADD, "endBound" : BoundingType.UP_TO_SURFACE, "oppositeDirection" : true, "endBoundEntityFace" : qUnion([Q1]), "depth" : 25 * mm});
        }
        {
            var Q0;
            Q0=makeQuery(id+"F21.imprint","IMPRINT",FACE,{"disambiguationData":[TD([[makeQuery(id+"F21.imprint","IMPRINT",EDGE,{"derivedFrom":sQuery(id+"F21.wireOp",EDGE,"E46")}),1.0]])]});
            extrude(context, id + "F48", {"entities" : qUnion([Q0]), "depth" : 12 * mm});
        }
        {
            var Q0;
            Q0=qCreatedBy(makeId("Top.planeOp"),FACE);
            var sketch = newSketch(context, id + "F49", { "sketchPlane" : qUnion([Q0])});
            skLineSegment(sketch, "E123.0", {"start": v(-168.92, -129.14) * mm, "end": v(168.92, -129.14) * mm, "construction": true});
            skLineSegment(sketch, "E124.0", {"start": v(196.3, -81.72) * mm, "end": v(168.92, -129.14) * mm, "construction": true});
            skLineSegment(sketch, "E125.0", {"start": v(-168.92, -129.14) * mm, "end": v(-196.3, -81.72) * mm, "construction": true});
            skLineSegment(sketch, "E126.0", {"start": v(-27.38, 210.86) * mm, "end": v(-196.3, -81.72) * mm, "construction": true});
            skLineSegment(sketch, "E127.0", {"start": v(-27.38, 210.86) * mm, "end": v(27.38, 210.86) * mm, "construction": true});
            skLineSegment(sketch, "E128.0", {"start": v(196.3, -81.72) * mm, "end": v(27.38, 210.86) * mm, "construction": true});
            skLineSegment(sketch, "E129.0", {"start": v(194, -81.72) * mm, "end": v(167.77, -127.14) * mm});
            skLineSegment(sketch, "E129.1", {"start": v(-26.22, 208.86) * mm, "end": v(26.22, 208.86) * mm});
            skLineSegment(sketch, "E129.2", {"start": v(-26.22, 208.86) * mm, "end": v(-194, -81.72) * mm});
            skLineSegment(sketch, "E129.3", {"start": v(194, -81.72) * mm, "end": v(26.22, 208.86) * mm});
            skLineSegment(sketch, "E129.4", {"start": v(-167.77, -127.14) * mm, "end": v(-194, -81.72) * mm});
            skLineSegment(sketch, "E129.5", {"start": v(-167.77, -127.14) * mm, "end": v(167.77, -127.14) * mm});
            skSolve(sketch);
        }
        {
            var Q0;
            Q0 = qSketchRegion(id + "F49", true);
            extrude(context, id + "F50", {"entities" : qUnion([Q0]), "depth" : 6 * mm});
        }
        {
            var Q0;
            Q0=makeQuery(id+"F50.opExtrude","CAP_FACE",FACE,{"disambiguationData":[OSD([sQuery(id+"F49.wireOp",EDGE,"E129.0"),sQuery(id+"F49.wireOp",EDGE,"E129.1"),sQuery(id+"F49.wireOp",EDGE,"E129.2"),sQuery(id+"F49.wireOp",EDGE,"E129.3"),sQuery(id+"F49.wireOp",EDGE,"E129.4"),sQuery(id+"F49.wireOp",EDGE,"E129.5")])],"isStart":true});
            var sketch = newSketch(context, id + "F51", { "sketchPlane" : qUnion([Q0])});
            skLineSegment(sketch, "E130.0", {"start": v(38.93, -230.86) * mm, "end": v(219.4, 81.72) * mm});
            skLineSegment(sketch, "E130.1", {"start": v(180.47, 149.14) * mm, "end": v(-180.47, 149.14) * mm});
            skLineSegment(sketch, "E130.2", {"start": v(-180.47, 149.14) * mm, "end": v(-219.4, 81.72) * mm});
            skLineSegment(sketch, "E130.3", {"start": v(219.4, 81.72) * mm, "end": v(180.47, 149.14) * mm});
            skLineSegment(sketch, "E130.4", {"start": v(-219.4, 81.72) * mm, "end": v(-38.93, -230.86) * mm});
            skLineSegment(sketch, "E130.5", {"start": v(-38.93, -230.86) * mm, "end": v(38.93, -230.86) * mm});
            skSolve(sketch);
        }
        {
            var Q0;
            Q0=makeQuery(id+"F51.imprint","IMPRINT",FACE,{"disambiguationData":[TD([[makeQuery(id+"F51.imprint","IMPRINT",EDGE,{"derivedFrom":sQuery(id+"F51.wireOp",EDGE,"E130.0")}),1.0]])]});
            var Q1;
            Q1=makeQuery(id+"F51.imprint","IMPRINT",FACE,{"disambiguationData":[TD([[makeQuery(id+"F51.imprint","IMPRINT",EDGE,{"derivedFrom":makeQuery(id+"F50.opExtrude","CAP_EDGE",EDGE,{"disambiguationData":[OSD([sQuery(id+"F49.wireOp",EDGE,"E129.0")])],"isStart":true})}),1.0]])]});
            extrude(context, id + "F52", {"entities" : qUnion([Q0, Q1]), "operationType" : NewBodyOperationType.ADD, "depth" : 6 * mm});
        }
        {
            var Q0;
            Q0=makeQuery(id+"F52.opExtrude","CAP_FACE",FACE,{"disambiguationData":[OSD([sQuery(id+"F51.wireOp",EDGE,"E130.0"),sQuery(id+"F51.wireOp",EDGE,"E130.1"),sQuery(id+"F51.wireOp",EDGE,"E130.2"),sQuery(id+"F51.wireOp",EDGE,"E130.3"),sQuery(id+"F51.wireOp",EDGE,"E130.4"),sQuery(id+"F51.wireOp",EDGE,"E130.5")])],"isStart":false});
            var sketch = newSketch(context, id + "F53", { "sketchPlane" : qUnion([Q0])});
            skCircle(sketch, "E131", {"center": v(0, 0) * mm, "radius": 12.5 * mm});
            skSolve(sketch);
        }
        {
            var Q0;
            Q0 = qSketchRegion(id + "F53", true);
            var Q1;
            Q1=makeQuery(id+"F50.opExtrude","CAP_FACE",FACE,{"disambiguationData":[OSD([sQuery(id+"F49.wireOp",EDGE,"E129.0"),sQuery(id+"F49.wireOp",EDGE,"E129.1"),sQuery(id+"F49.wireOp",EDGE,"E129.2"),sQuery(id+"F49.wireOp",EDGE,"E129.3"),sQuery(id+"F49.wireOp",EDGE,"E129.4"),sQuery(id+"F49.wireOp",EDGE,"E129.5")])],"isStart":false});
            extrude(context, id + "F54", {"entities" : qUnion([Q0]), "operationType" : NewBodyOperationType.REMOVE, "endBound" : BoundingType.UP_TO_SURFACE, "oppositeDirection" : true, "endBoundEntityFace" : qUnion([Q1]), "depth" : 25 * mm});
        }
        {
            var Q0;
            Q0=makeQuery(id+"F48.opExtrude","SWEPT_FACE",FACE,{"disambiguationData":[OSD([sQuery(id+"F21.wireOp",EDGE,"E51.2.1")])]});
            var sketch = newSketch(context, id + "F55", { "sketchPlane" : qUnion([Q0])});
            skLineSegment(sketch, "E132.bottom", {"start": v(-205.9, 488) * mm, "end": v(205.9, 488) * mm});
            skLineSegment(sketch, "E132.top", {"start": v(-205.9, 494) * mm, "end": v(205.9, 494) * mm});
            skLineSegment(sketch, "E132.left", {"start": v(-205.9, 488) * mm, "end": v(-205.9, 494) * mm});
            skLineSegment(sketch, "E132.right", {"start": v(205.9, 488) * mm, "end": v(205.9, 494) * mm});
            skSolve(sketch);
        }
        {
            var Q0;
            Q0 = qSketchRegion(id + "F55", true);
            extrude(context, id + "F56", {"entities" : qUnion([Q0]), "operationType" : NewBodyOperationType.REMOVE, "oppositeDirection" : true, "depth" : 14 * mm});
        }
        {
            var Q0;
            Q0=makeQuery(id+"F48.opExtrude","SWEPT_FACE",FACE,{"disambiguationData":[OSD([sQuery(id+"F21.wireOp",EDGE,"E49")])]});
            var sketch = newSketch(context, id + "F57", { "sketchPlane" : qUnion([Q0])});
            skLineSegment(sketch, "E133.bottom", {"start": v(-205.9, 488) * mm, "end": v(205.9, 488) * mm});
            skLineSegment(sketch, "E133.top", {"start": v(-205.9, 494) * mm, "end": v(205.9, 494) * mm});
            skLineSegment(sketch, "E133.left", {"start": v(-205.9, 488) * mm, "end": v(-205.9, 494) * mm});
            skLineSegment(sketch, "E133.right", {"start": v(205.9, 488) * mm, "end": v(205.9, 494) * mm});
            skSolve(sketch);
        }
        {
            var Q0;
            Q0 = qSketchRegion(id + "F57", true);
            extrude(context, id + "F58", {"entities" : qUnion([Q0]), "operationType" : NewBodyOperationType.REMOVE, "oppositeDirection" : true, "depth" : 14 * mm});
        }
        {
            var Q0;
            Q0=makeQuery(id+"F48.opExtrude","SWEPT_FACE",FACE,{"disambiguationData":[OSD([sQuery(id+"F21.wireOp",EDGE,"E51.1.1")])]});
            var sketch = newSketch(context, id + "F59", { "sketchPlane" : qUnion([Q0])});
            skLineSegment(sketch, "E134.bottom", {"start": v(-205.9, 488) * mm, "end": v(205.9, 488) * mm});
            skLineSegment(sketch, "E134.top", {"start": v(-205.9, 494) * mm, "end": v(205.9, 494) * mm});
            skLineSegment(sketch, "E134.left", {"start": v(-205.9, 488) * mm, "end": v(-205.9, 494) * mm});
            skLineSegment(sketch, "E134.right", {"start": v(205.9, 488) * mm, "end": v(205.9, 494) * mm});
            skSolve(sketch);
        }
        {
            var Q0;
            Q0 = qSketchRegion(id + "F59", true);
            extrude(context, id + "F60", {"entities" : qUnion([Q0]), "operationType" : NewBodyOperationType.REMOVE, "oppositeDirection" : true, "depth" : 14 * mm});
        }
    });
